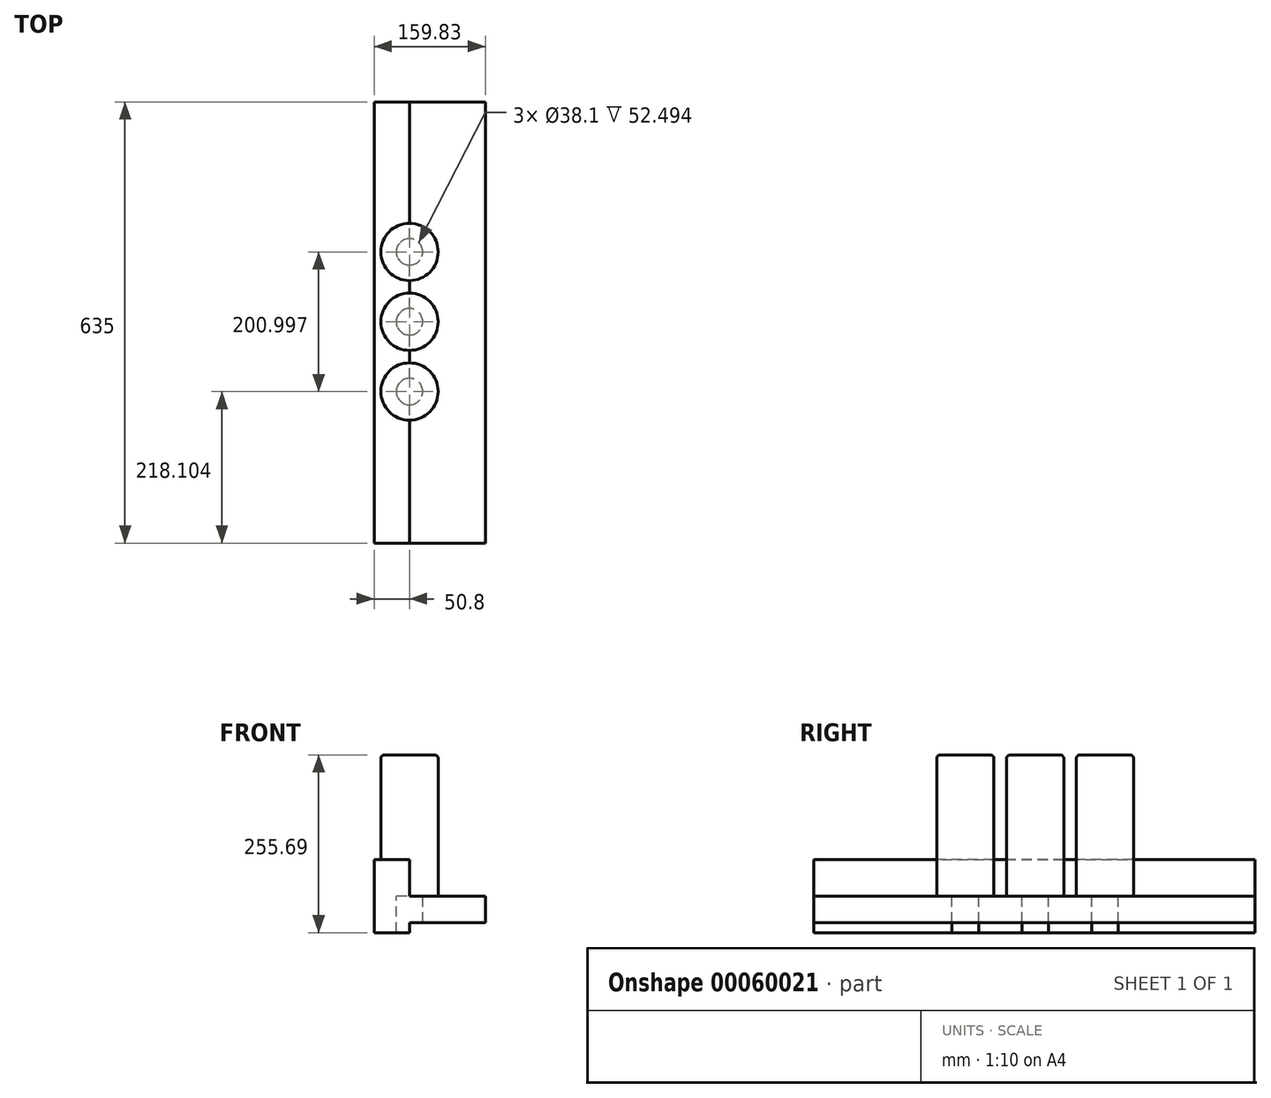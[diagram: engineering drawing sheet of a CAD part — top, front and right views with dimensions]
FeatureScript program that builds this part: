
annotation { "Feature Type Name" : "Feature", "Feature Type Description" : "" }
export const myFeature = defineFeature(function(context is Context, id is Id, definition is map)
    precondition{}
    {
        {
            var Q0;
            Q0=qCreatedBy(makeId("Front.planeOp"),FACE);
            var sketch = newSketch(context, id + "F0", { "sketchPlane" : qUnion([Q0])});
            skLineSegment(sketch, "E0.bottom", {"start": v(-50.8, 52.5) * mm, "end": v(0, 52.5) * mm});
            skLineSegment(sketch, "E0.top", {"start": v(-50.8, -52.5) * mm, "end": v(0, -52.5) * mm});
            skLineSegment(sketch, "E0.left", {"start": v(-50.8, 52.5) * mm, "end": v(-50.8, -52.5) * mm});
            skLineSegment(sketch, "E0.right", {"start": v(0, 52.5) * mm, "end": v(0, -52.5) * mm});
            skLineSegment(sketch, "E1.bottom", {"start": v(-43.37, 0) * mm, "end": v(109.03, 0) * mm});
            skLineSegment(sketch, "E1.top", {"start": v(-43.37, -38.1) * mm, "end": v(109.03, -38.1) * mm});
            skLineSegment(sketch, "E1.left", {"start": v(-43.37, 0) * mm, "end": v(-43.37, -38.1) * mm});
            skLineSegment(sketch, "E1.right", {"start": v(109.03, 0) * mm, "end": v(109.03, -38.1) * mm});
            skSolve(sketch);
        }
        {
            var Q0;
            {var subQ5=sQuery(id+"F0.wireOp",EDGE,"E1.right");Q0=makeQuery(id+"F0.imprint","IMPRINT",FACE,{"disambiguationData":[TD([[makeQuery(id+"F0.imprint","IMPRINT",EDGE,{"derivedFrom":subQ5}),-1.0]])]});}
            var Q1;
            {var subQ0=sQuery(id+"F0.wireOp",EDGE,"E1.bottom");var subQ1=sQuery(id+"F0.wireOp",EDGE,"E0.left");var subQ2=makeQuery(id+"F0.imprint","INTERSECT",VERTEX,{"derivedFrom":[subQ1,subQ0]});Q1=makeQuery(id+"F0.imprint","IMPRINT",FACE,{"disambiguationData":[TD([[makeQuery(id+"F0.imprint","IMPRINT",EDGE,{"disambiguationData":[TD([[subQ2,-1.0]])],"derivedFrom":subQ1}),1.0]])]});}
            var Q2;
            {var subQ5=sQuery(id+"F0.wireOp",EDGE,"E1.left");Q2=makeQuery(id+"F0.imprint","IMPRINT",FACE,{"disambiguationData":[TD([[makeQuery(id+"F0.imprint","IMPRINT",EDGE,{"derivedFrom":subQ5}),1.0]])]});}
            extrude(context, id + "F1", {"entities" : qUnion([Q0, Q1, Q2]), "depth" : 635 * mm});
        }
        {
            var Q0;
            Q0=makeQuery(id+"F1.opExtrude","SWEPT_FACE",FACE,{"disambiguationData":[OSD([sQuery(id+"F0.wireOp",EDGE,"E1.bottom")])]});
            var sketch = newSketch(context, id + "F2", { "sketchPlane" : qUnion([Q0])});
            skCircle(sketch, "E2", {"center": v(0, -215.9) * mm, "radius": 41.24 * mm});
            skCircle(sketch, "E3", {"center": v(0, -316.4) * mm, "radius": 41.24 * mm});
            skCircle(sketch, "E4", {"center": v(0, -416.9) * mm, "radius": 41.24 * mm});
            skLineSegment(sketch, "E5", {"start": v(0, -215.9) * mm, "end": v(0, -316.4) * mm});
            skLineSegment(sketch, "E6", {"start": v(0, -316.4) * mm, "end": v(0, -416.9) * mm});
            skSolve(sketch);
        }
        {
            var Q0;
            Q0=makeQuery(id+"F2.imprint","IMPRINT",FACE,{"disambiguationData":[TD([[makeQuery(id+"F2.imprint","IMPRINT",EDGE,{"derivedFrom":sQuery(id+"F2.wireOp",EDGE,"E2")}),1.0]])]});
            var Q1;
            {var subQ0=sQuery(id+"F2.wireOp",EDGE,"E5");var subQ1=sQuery(id+"F2.wireOp",EDGE,"E3");var subQ2=makeQuery(id+"F2.imprint","INTERSECT",VERTEX,{"derivedFrom":[subQ1,subQ0]});Q1=makeQuery(id+"F2.imprint","IMPRINT",FACE,{"disambiguationData":[TD([[makeQuery(id+"F2.imprint","IMPRINT",EDGE,{"disambiguationData":[TD([[subQ2,1.0]])],"derivedFrom":subQ1}),1.0]])]});}
            var Q2;
            Q2=makeQuery(id+"F2.imprint","IMPRINT",FACE,{"disambiguationData":[TD([[makeQuery(id+"F2.imprint","IMPRINT",EDGE,{"derivedFrom":sQuery(id+"F2.wireOp",EDGE,"E4")}),1.0]])]});
            var Q3;
            {var subQ0=sQuery(id+"F2.wireOp",EDGE,"E5");var subQ1=sQuery(id+"F2.wireOp",EDGE,"E3");var subQ2=makeQuery(id+"F2.imprint","INTERSECT",VERTEX,{"derivedFrom":[subQ1,subQ0]});Q3=makeQuery(id+"F2.imprint","IMPRINT",FACE,{"disambiguationData":[TD([[makeQuery(id+"F2.imprint","IMPRINT",EDGE,{"disambiguationData":[TD([[subQ2,-1.0]])],"derivedFrom":subQ1}),1.0]])]});}
            extrude(context, id + "F3", {"entities" : qUnion([Q0, Q1, Q2, Q3]), "operationType" : NewBodyOperationType.ADD, "depth" : 203.2 * mm});
        }
        {
            var Q0;
            Q0=makeQuery(id+"F3.opExtrude","CAP_EDGE",EDGE,{"disambiguationData":[OSD([sQuery(id+"F2.wireOp",EDGE,"E2")])],"isStart":false});
            var Q1;
            Q1=makeQuery(id+"F3.opExtrude","CAP_EDGE",EDGE,{"disambiguationData":[OSD([sQuery(id+"F2.wireOp",EDGE,"E3")])],"isStart":false});
            var Q2;
            Q2=makeQuery(id+"F3.opExtrude","CAP_EDGE",EDGE,{"disambiguationData":[OSD([sQuery(id+"F2.wireOp",EDGE,"E4")])],"isStart":false});
            fillet(context, id + "F4", {"entities" : qUnion([Q0, Q1, Q2]), "radius" : 5.08 * mm, "tangentPropagation" : true, "allowEdgeOverflow" : false});
        }
        {
            var Q0;
            Q0=sQuery(id+"F2.wireOp",VERTEX,"E2.center");
            var Q1;
            Q1=sQuery(id+"F2.wireOp",VERTEX,"E3.center");
            var Q2;
            Q2=sQuery(id+"F2.wireOp",VERTEX,"E4.center");
            var Q3;
            Q3=makeQuery(id+"F1.opExtrude","SWEPT_BODY",BODY,{"disambiguationData":[OSD([sQuery(id+"F0.wireOp",EDGE,"E1.bottom"),sQuery(id+"F0.wireOp",EDGE,"E1.top"),sQuery(id+"F0.wireOp",EDGE,"E1.left"),sQuery(id+"F0.wireOp",EDGE,"E1.right")])]});
            hole(context, id + "F5", {"style" : HoleStyle.SIMPLE, "holeDiameter" : 38.1 * mm, "endStyle" : HoleEndStyle.BLIND, "holeDepth" : 508 * mm, "locations" : qUnion([Q0, Q1, Q2]), "scope" : qUnion([Q3])});
        }
    });
